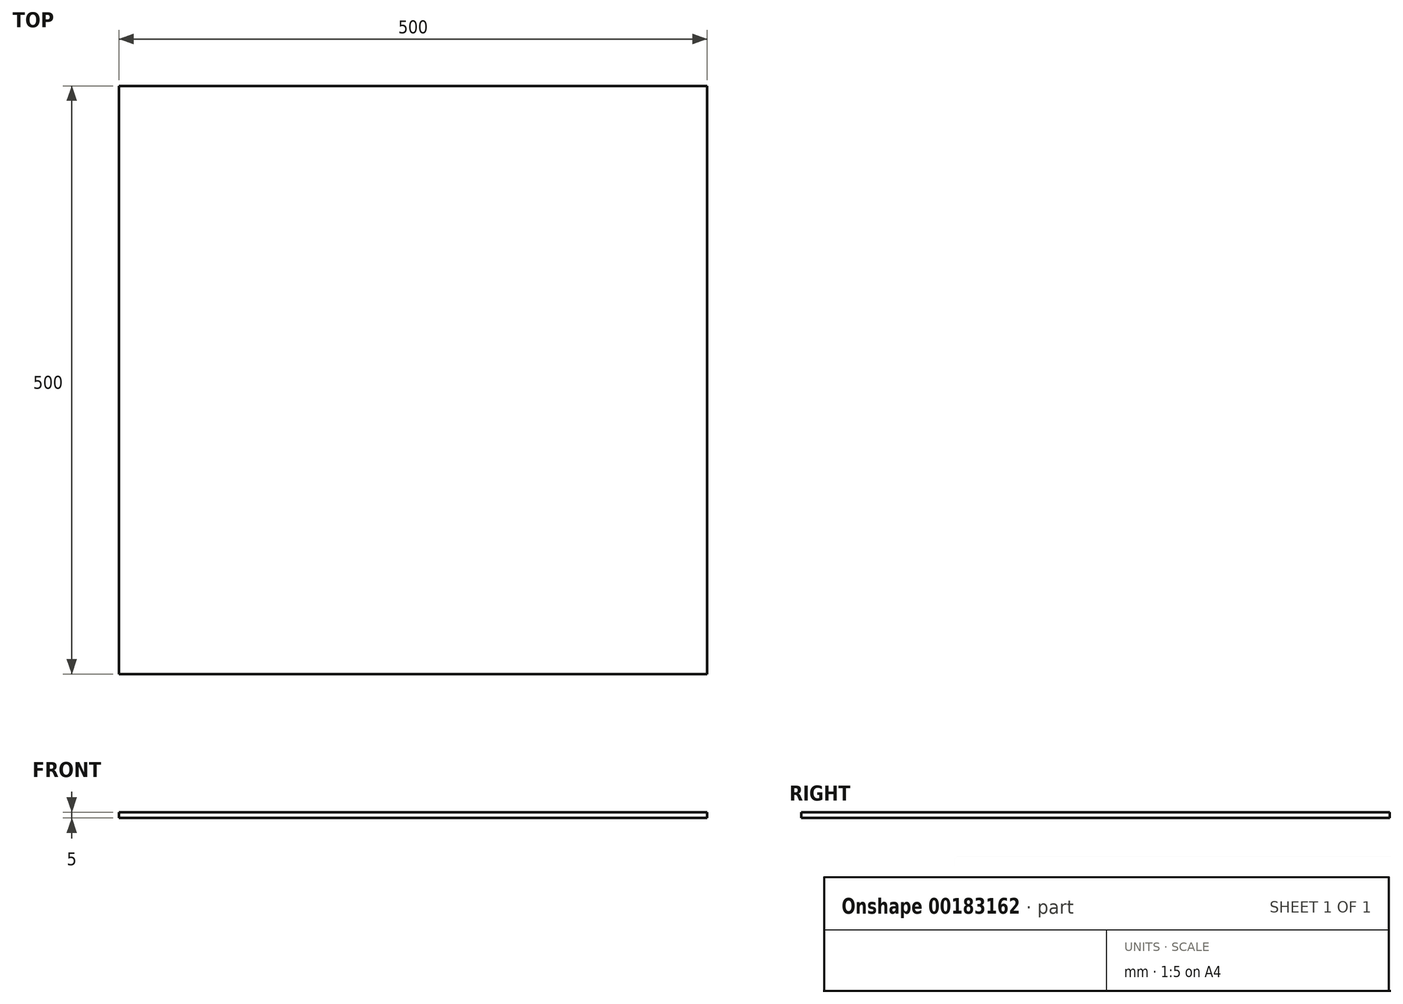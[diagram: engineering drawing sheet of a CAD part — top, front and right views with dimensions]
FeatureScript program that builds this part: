
annotation { "Feature Type Name" : "Feature", "Feature Type Description" : "" }
export const myFeature = defineFeature(function(context is Context, id is Id, definition is map)
    precondition{}
    {
        {
            var Q0;
            Q0=qCreatedBy(makeId("Top.planeOp"),FACE);
            var sketch = newSketch(context, id + "F0", { "sketchPlane" : qUnion([Q0])});
            skLineSegment(sketch, "E0.bottom", {"start": v(0, 0) * mm, "end": v(500, 0) * mm});
            skLineSegment(sketch, "E0.top", {"start": v(0, 500) * mm, "end": v(500, 500) * mm});
            skLineSegment(sketch, "E0.left", {"start": v(0, 0) * mm, "end": v(0, 500) * mm});
            skLineSegment(sketch, "E0.right", {"start": v(500, 0) * mm, "end": v(500, 500) * mm});
            skSolve(sketch);
        }
        {
            var Q0;
            Q0 = qSketchRegion(id + "F0", true);
            extrude(context, id + "F1", {"entities" : qUnion([Q0]), "depth" : 5 * mm});
        }
    });
